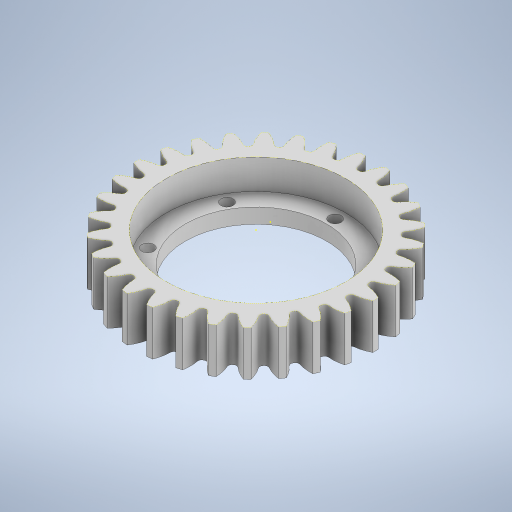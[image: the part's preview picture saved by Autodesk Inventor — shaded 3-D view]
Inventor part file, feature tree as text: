
AUTODESK INVENTOR PART (.ipt)
format: ipt  version: 2024 (Build 280153000, 153)  size: 598,016 bytes
history: native  units: mm
features: sketch x5, extrude x3, pattern_circular x1
ambient origin geometry x8: Origin, YZ Plane, XZ Plane, XY Plane, X Axis, Y Axis, Z Axis, Center Point
bodies: Solid1 (feature_tree)
feature tree (9):
  extrude  "Extrusion1"  Depth=30.0mm TaperAngle=0.0deg
  extrude  "Extrusion2"  Depth=20.0mm TaperAngle=0.0deg
  sketch  "Sketch3"  dims[d11=30.0mm d12=0.0mm d13=300.0mm d14=360.0deg]
  extrude  "Extrusion3"  Depth=300.0mm TaperAngle=360.0deg
  pattern_circular  "Circular Pattern1"  [2 undecoded]
  sketch  "Sketch5"
  sketch  "Sketch1"  dims[d1=60.0mm d2=125.0mm d3=106.0mm d4=360.0deg d5=8.1mm d6=30.0mm d7=0.0mm]
  sketch  "Sketch2"  dims[d8=120.000028mm d9=20.0mm d10=0.0mm]
  sketch  "Sketch4"
note: 2 required parameter values undecoded (feature->parameter linkage not recoverable at this tier; creation-order binding heuristic only, values carry confidence <= 0.55)
